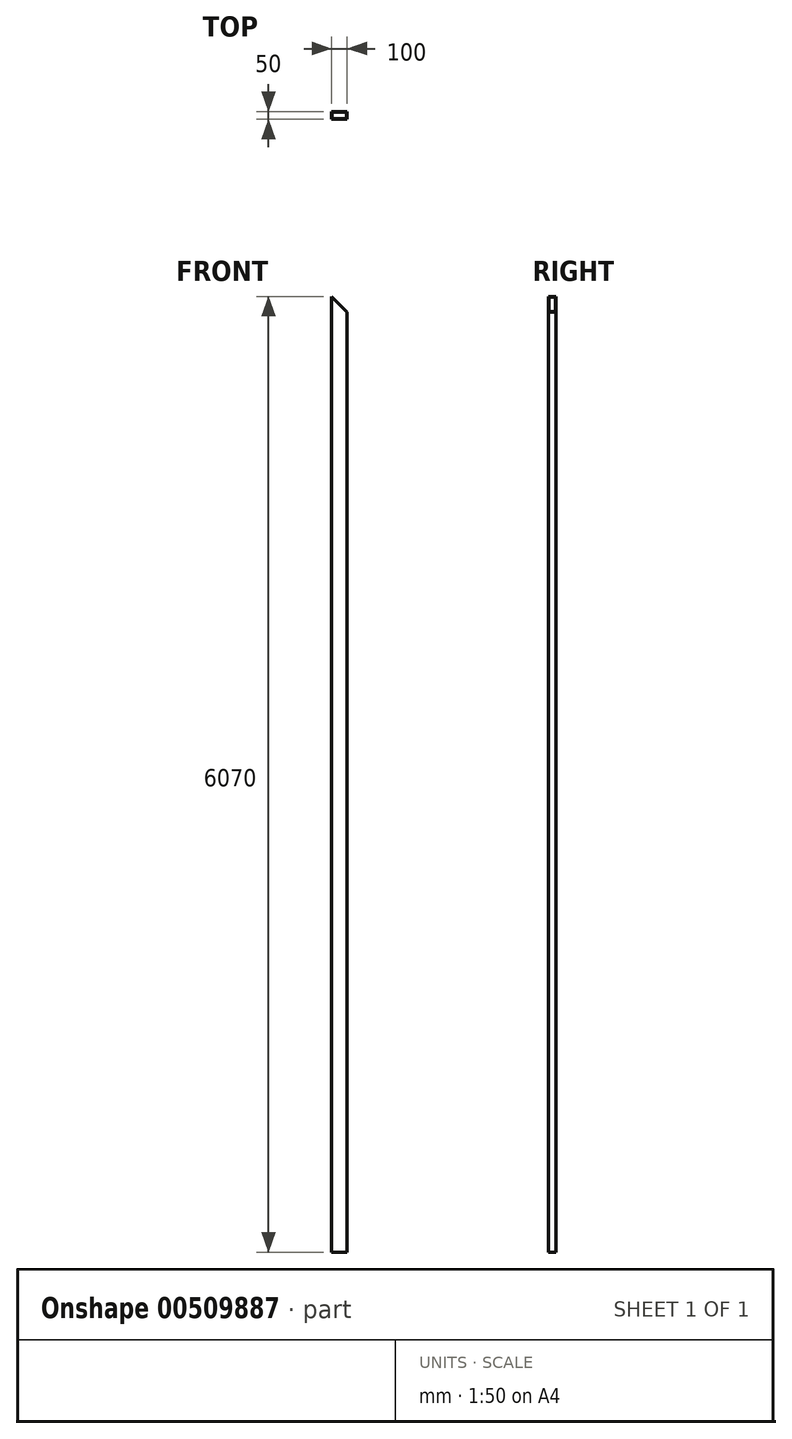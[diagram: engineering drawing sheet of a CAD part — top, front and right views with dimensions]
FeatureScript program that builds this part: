
annotation { "Feature Type Name" : "Feature", "Feature Type Description" : "" }
export const myFeature = defineFeature(function(context is Context, id is Id, definition is map)
    precondition{}
    {
        {
            var Q0;
            Q0=qCreatedBy(makeId("Top.planeOp"),FACE);
            var sketch = newSketch(context, id + "F0", { "sketchPlane" : qUnion([Q0])});
            skLineSegment(sketch, "E0.bottom", {"start": v(46.8, -25) * mm, "end": v(-53.2, -25) * mm});
            skLineSegment(sketch, "E0.top", {"start": v(46.8, 25) * mm, "end": v(-53.2, 25) * mm});
            skLineSegment(sketch, "E0.left", {"start": v(46.8, -25) * mm, "end": v(46.8, 25) * mm});
            skLineSegment(sketch, "E0.right", {"start": v(-53.2, -25) * mm, "end": v(-53.2, 25) * mm});
            skPoint(sketch, "E0.middle", {"position": v(-3.2, 0) * mm});
            skLineSegment(sketch, "E1.bottom", {"start": v(43.8, -22) * mm, "end": v(-50.2, -22) * mm});
            skLineSegment(sketch, "E1.top", {"start": v(43.8, 22) * mm, "end": v(-50.2, 22) * mm});
            skLineSegment(sketch, "E1.left", {"start": v(43.8, -22) * mm, "end": v(43.8, 22) * mm});
            skLineSegment(sketch, "E1.right", {"start": v(-50.2, -22) * mm, "end": v(-50.2, 22) * mm});
            skSolve(sketch);
        }
        {
            var Q0;
            Q0=makeQuery(id+"F0.imprint","IMPRINT",FACE,{"disambiguationData":[TD([[makeQuery(id+"F0.imprint","IMPRINT",EDGE,{"derivedFrom":sQuery(id+"F0.wireOp",EDGE,"E0.bottom")}),-1.0]])]});
            extrude(context, id + "F1", {"entities" : qUnion([Q0]), "depth" : 6070 * mm, "offsetDistance" : 25 * mm});
        }
        {
            var Q0;
            Q0=makeQuery(id+"F1.opExtrude","CAP_EDGE",EDGE,{"disambiguationData":[OSD([sQuery(id+"F0.wireOp",EDGE,"E0.left")])],"isStart":false});
            chamfer(context, id + "F2", {"entities" : qUnion([Q0]), "width" : 100 * mm, "tangentPropagation" : true});
        }
    });
